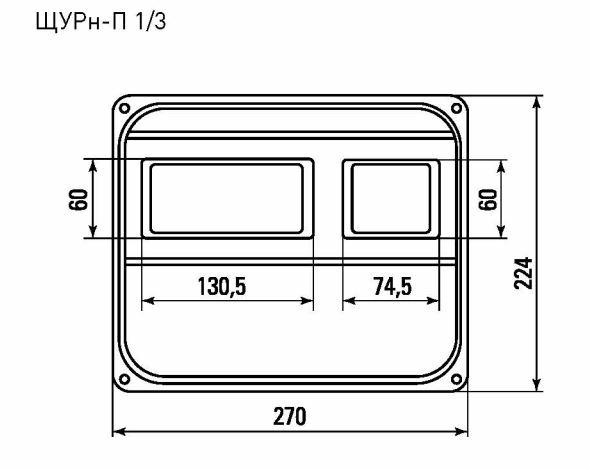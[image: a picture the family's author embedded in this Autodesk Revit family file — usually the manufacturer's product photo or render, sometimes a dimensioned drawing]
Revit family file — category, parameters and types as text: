
# Revit family: EKF_EE_КаркасВРУ-1UnitR_IP31_PROxima
name_source: partatom
category: Электрооборудование
units: mm (PartAtom-declared; Revit-internal decimal feet)

## family parameters
Всегда вертикально = Нет
На основе рабочей плоскости = Да
Общий = Да
При загрузке вырезать с полостями = Нет
Размер круглого соединителя = Использовать диаметр
Тип детали = Силовой щит
Точка расчета площади = Нет

## types (6) — shared parameters
ADSK_Единица измерения = шт.
ADSK_Завод-изготовитель = EKF
ADSK_Количество = 1
ADSK_Марка = Каркас ВРУ-1 Unit R
ADSK_Материал = RAL 7035_Сталь
ADSK_Обозначение = Каркас ВРУ-1 Unit R
ADSK_Размер_Глубина = 450 мм
D = 9 мм
t = 1 мм
ВертПроф_Отступ = 30 мм
Изготовитель = EKF
Отступ = 20 мм
РейкаПопереч_Шаг = 759 мм
Серия номенклатуры = Unit PROxima
Степень защиты IP = IP31
Стойка_a = 24 мм
ТВ = EKF_2
Тип установки = Напольный
Ц450х450 = Вл_EKF_EE_ЦокольВРУUNIT_PROxima : Цоколь к ВРУ Unit S IP31 (Вх450х450) EKF PROxima
Ц600х450 = Вл_EKF_EE_ЦокольВРУUNIT_PROxima : Цоколь к ВРУ Unit S IP31 (Вх600х450) EKF PROxima
Ц600х600 = Вл_EKF_EE_ЦокольВРУUNIT_PROxima : Цоколь к ВРУ Unit S IP31 (Вх600х600) EKF PROxima
Ц800х450 = Вл_EKF_EE_ЦокольВРУUNIT_PROxima : Цоколь к ВРУ Unit S IP31 (Вх800х450) EKF PROxima
Ц800х600 = Вл_EKF_EE_ЦокольВРУUNIT_PROxima : Цоколь к ВРУ Unit S IP31 (Вх800х600) EKF PROxima
zero-valued in all types: ADSK_Масса, Отметка по умолчанию

## per-type parameters (varying)
| type | ADSK_Код изделия | ADSK_Наименование | ADSK_Размер_Высота | ADSK_Размер_Ширина | Стойка_h | Тип | Цоколь |
| Каркас ВРУ-1 Unit R разборный (1800х450х450)  IP31 EKF PROxima | mb09-01-01 | Каркас ВРУ-1 Unit R разборный (1800х450х450) IP31 EKF PROxima | 1800 мм | 450 мм | 1780 мм | 85 мм | Вл_EKF_EE_ЦокольВРУUNIT_PROxima : Цоколь к ВРУ Unit S IP31 (Вх450х450) EKF PROxima |
| Каркас ВРУ-1 Unit R разборный (1800х600х450)  IP31 EKF PROxima | mb09-01-02 | Каркас ВРУ-1 Unit R разборный (1800х600х450) IP31 EKF PROxima | 1800 мм | 600 мм | 1780 мм | 86 мм | Вл_EKF_EE_ЦокольВРУUNIT_PROxima : Цоколь к ВРУ Unit S IP31 (Вх600х450) EKF PROxima |
| Каркас ВРУ-1 Unit R разборный (1800х800х450)  IP31 EKF PROxima | mb09-01-03 | Каркас ВРУ-1 Unit R разборный (1800х800х450) IP31 EKF PROxima | 1800 мм | 800 мм | 1780 мм | 87 мм | Вл_EKF_EE_ЦокольВРУUNIT_PROxima : Цоколь к ВРУ Unit S IP31 (Вх800х450) EKF PROxima |
| Каркас ВРУ-1 Unit R разборный (2000х450х450)  IP31 EKF PROxima | mb09-01-04 | Каркас ВРУ-1 Unit R разборный (2000х450х450) IP31 EKF PROxima | 2000 мм | 450 мм | 1980 мм | 88 мм | Вл_EKF_EE_ЦокольВРУUNIT_PROxima : Цоколь к ВРУ Unit S IP31 (Вх450х450) EKF PROxima |
| Каркас ВРУ-1 Unit R разборный (2000х600х450)  IP31 EKF PROxima | mb09-01-05 | Каркас ВРУ-1 Unit R разборный (2000х600х450) IP31 EKF PROxima | 2000 мм | 600 мм | 1980 мм | 89 мм | Вл_EKF_EE_ЦокольВРУUNIT_PROxima : Цоколь к ВРУ Unit S IP31 (Вх600х450) EKF PROxima |
| Каркас ВРУ-1 Unit R разборный (2000х800х450)  IP31 EKF PROxima | mb09-01-06 | Каркас ВРУ-1 Unit R разборный (2000х800х450) IP31 EKF PROxima | 2000 мм | 800 мм | 1980 мм | 90 мм | Вл_EKF_EE_ЦокольВРУUNIT_PROxima : Цоколь к ВРУ Unit S IP31 (Вх800х450) EKF PROxima |
